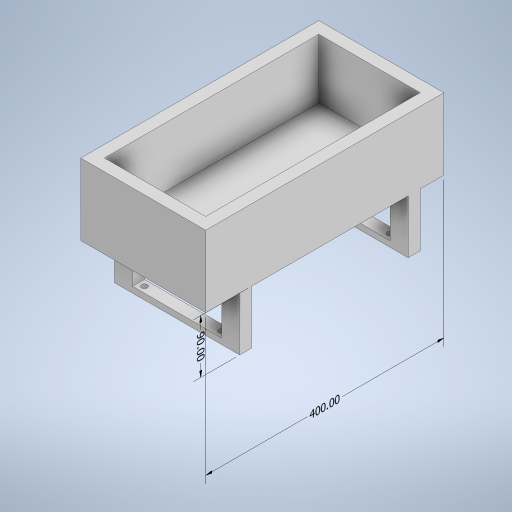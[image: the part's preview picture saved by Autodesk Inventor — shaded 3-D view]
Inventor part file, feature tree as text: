
AUTODESK INVENTOR PART (.ipt)
format: ipt  version: 2023 (Build 270158000, 158)  size: 323,072 bytes
history: native  units: mm
features: extrude x7, sketch x7, other x4
ambient origin geometry x8: Origin, YZ Plane, XZ Plane, XY Plane, X Axis, Y Axis, Z Axis, Center Point
bodies: Body1 (feature_tree)
feature tree (18):
  other  "Sólido1"
  other  "Anotaciones"
  extrude  "Extrusión1"  Depth=400.0mm
  extrude  "Extrusión2"  Depth=170.0mm
  extrude  "Extrusión3"  Depth=100.0mm TaperAngle=0.0deg
  extrude  "Extrusión4"  Depth=20.0mm
  extrude  "Extrusión5"  Depth=10.0mm
  sketch  "Boceto8"  dims[d17=150.0mm d18=0.0mm d19=10.0mm]
  sketch  "Boceto9"  dims[d20=150.0mm d21=0.0mm d22=10.0mm d23=10.0mm d24=40.0mm d25=40.0mm d26=10.0mm d27=10.0mm d28=40.0mm d29=40.0mm d30=20.0mm d31=0.0mm d32=20.0mm d33=0.0mm d34=57.0mm d35=57.0mm d36=20.0mm d37=40.0mm d38=40.0mm d39=10.0mm d40=10.0mm d41=1.984831mm d42=5.975724mm d43=90.0mm d44=5.94019mm d45=5.025575mm d46=400.0mm]
  extrude  "Extrusión6"  Depth=10.0mm
  extrude  "Extrusión7"  Depth=10.0mm
  sketch  "Boceto1"  dims[d0=210.0mm d1=400.0mm]
  sketch  "Boceto2"  dims[d2=120.0mm d3=0.0mm d4=170.0mm]
  sketch  "Boceto3"  dims[d5=360.0mm d6=100.0mm d7=0.0mm]
  sketch  "Boceto6"  dims[d9=20.0mm d12=20.0mm]
  sketch  "Boceto7"  dims[d14=90.0mm d15=0.0mm d16=10.0mm]
  other  "Cota lineal 1"
  other  "Cota lineal 2"
